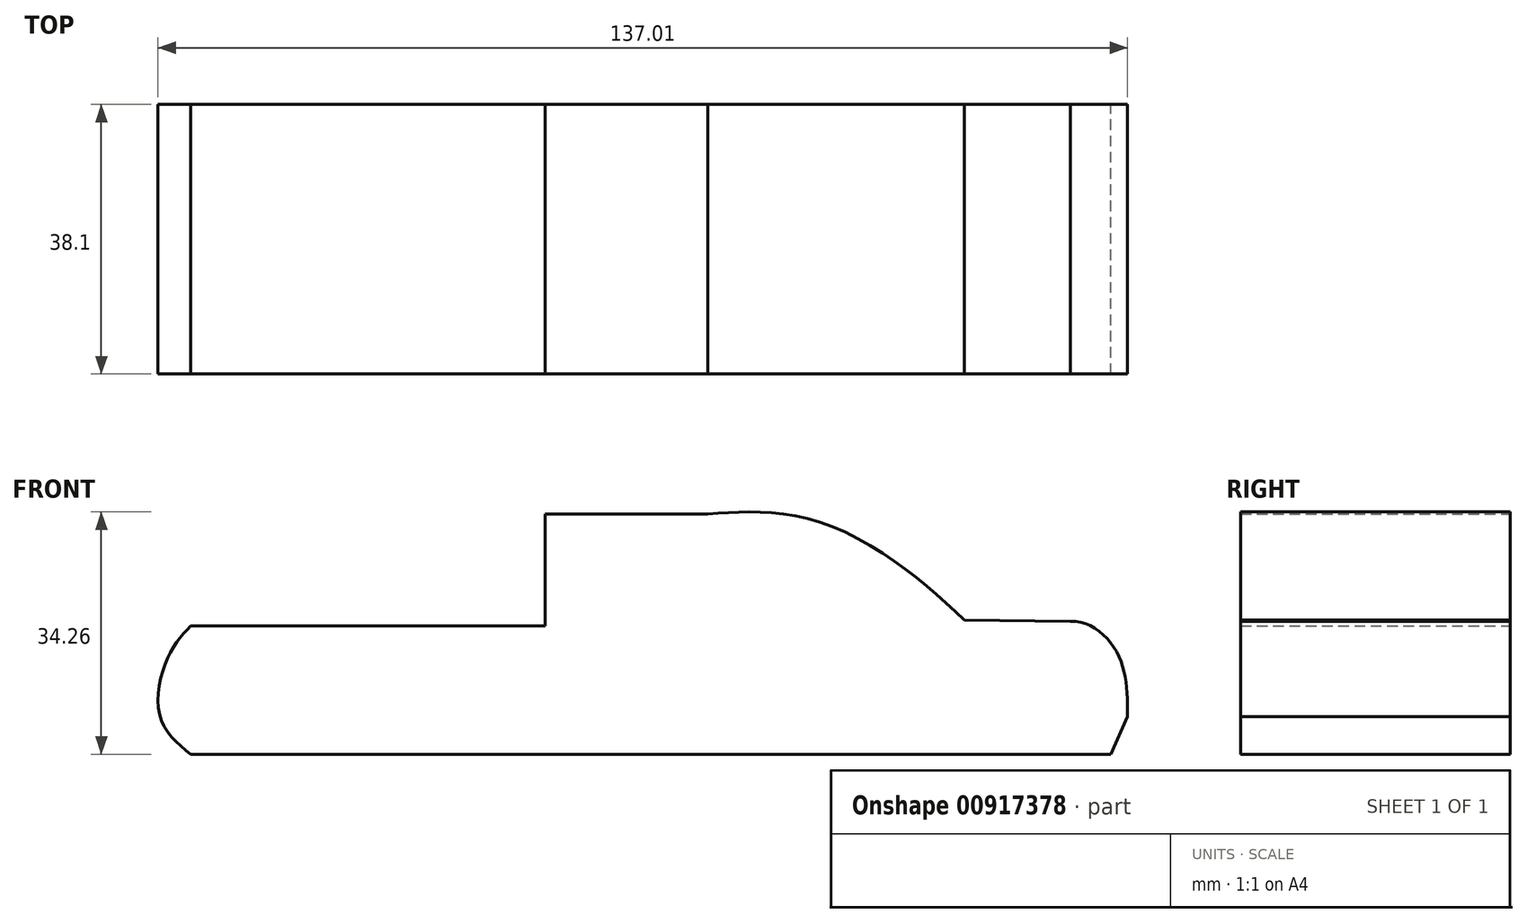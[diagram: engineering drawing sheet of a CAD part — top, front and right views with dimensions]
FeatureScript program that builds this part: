
annotation { "Feature Type Name" : "Feature", "Feature Type Description" : "" }
export const myFeature = defineFeature(function(context is Context, id is Id, definition is map)
    precondition{}
    {
        {
            var Q0;
            Q0=qCreatedBy(makeId("Front.planeOp"),FACE);
            var sketch = newSketch(context, id + "F0", { "sketchPlane" : qUnion([Q0])});
            skFitSpline(sketch, "E0", {"points": [v(68.66, 0) * mm, v(67.1, 9.2) * mm, v(60.6, 13.46) * mm], "startDerivative": vector(0.3, 20.02) * mm, "endDerivative": vector(-16.9, -1.31) * mm});
            skLineSegment(sketch, "E1", {"start": v(60.6, 13.46) * mm, "end": v(45.62, 13.67) * mm});
            skFitSpline(sketch, "E2", {"points": [v(45.62, 13.67) * mm, v(37.27, 20.87) * mm, v(26.05, 27.2) * mm, v(16.55, 28.92) * mm, v(9.35, 28.64) * mm], "startDerivative": vector(-29.94, 27.89) * mm, "endDerivative": vector(-33.05, -2.59) * mm});
            skLineSegment(sketch, "E3", {"start": v(9.35, 28.64) * mm, "end": v(0, 28.64) * mm});
            skLineSegment(sketch, "E4", {"start": v(0, 28.64) * mm, "end": v(-13.67, 28.64) * mm});
            skLineSegment(sketch, "E5", {"start": v(-13.67, 28.64) * mm, "end": v(-13.67, 12.8) * mm});
            skLineSegment(sketch, "E6", {"start": v(-13.67, 12.8) * mm, "end": v(-63.75, 12.8) * mm});
            skFitSpline(sketch, "E7", {"points": [v(-63.75, 12.8) * mm, v(-66.91, 8.5) * mm, v(-68.07, 0) * mm, v(-63.75, -5.32) * mm], "startDerivative": vector(-11.57, -12.3) * mm, "endDerivative": vector(16.5, -13.67) * mm});
            skFitSpline(sketch, "E8", {"points": [v(68.66, 0) * mm, v(66.34, -5.32) * mm], "startDerivative": vector(-2.32, -5.32) * mm, "endDerivative": vector(-2.32, -5.32) * mm});
            skLineSegment(sketch, "E9", {"start": v(-63.75, -5.32) * mm, "end": v(66.34, -5.32) * mm});
            skSolve(sketch);
        }
        {
            var Q0;
            Q0 = qSketchRegion(id + "F0", true);
            extrude(context, id + "F1", {"entities" : qUnion([Q0]), "depth" : 38.1 * mm, "offsetDistance" : 25.4 * mm});
        }
    });
